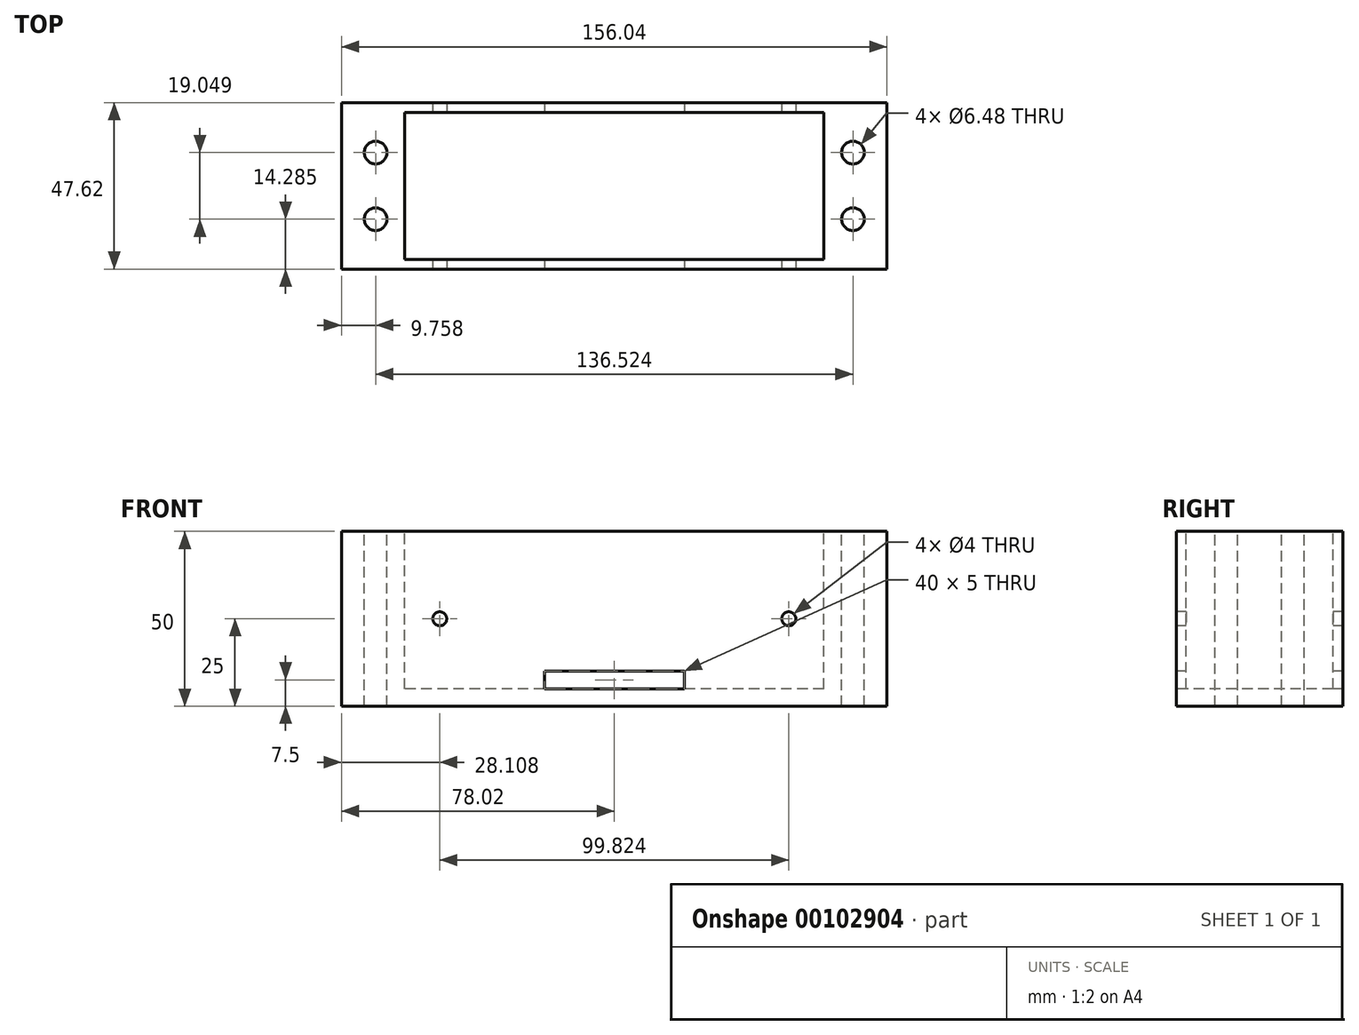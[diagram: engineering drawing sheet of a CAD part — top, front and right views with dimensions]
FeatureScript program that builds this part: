
annotation { "Feature Type Name" : "Feature", "Feature Type Description" : "" }
export const myFeature = defineFeature(function(context is Context, id is Id, definition is map)
    precondition{}
    {
        {
            var Q0;
            Q0=qCreatedBy(makeId("Top.planeOp"),FACE);
            var sketch = newSketch(context, id + "F0", { "sketchPlane" : qUnion([Q0])});
            skLineSegment(sketch, "E0", {"start": v(72.22, -23.01) * mm, "end": v(72.22, -15.86) * mm});
            skLineSegment(sketch, "E1", {"start": v(72.22, -3.19) * mm, "end": v(72.22, 3.17) * mm});
            skLineSegment(sketch, "E2", {"start": v(-68.2, -15.87) * mm, "end": v(-72.23, -15.87) * mm});
            skLineSegment(sketch, "E3", {"start": v(-68.26, 15.87) * mm, "end": v(-72.23, 15.87) * mm});
            skLineSegment(sketch, "E4", {"start": v(68.26, 15.87) * mm, "end": v(72.22, 15.87) * mm});
            skLineSegment(sketch, "E5", {"start": v(-68.26, 3.17) * mm, "end": v(-72.23, 3.17) * mm});
            skLineSegment(sketch, "E6", {"start": v(68.26, 3.17) * mm, "end": v(72.22, 3.17) * mm});
            skLineSegment(sketch, "E7", {"start": v(67.83, -3.19) * mm, "end": v(72.22, -3.19) * mm});
            skArc(sketch, "E8", {"start": v(67.83, -3.19) * mm, "mid": v(61.93, -9.96) * mm, "end": v(68.7, -15.86) * mm});
            skLineSegment(sketch, "E9", {"start": v(68.7, -15.86) * mm, "end": v(72.22, -15.86) * mm});
            skLineSegment(sketch, "E10", {"start": v(-68.33, -3.17) * mm, "end": v(-72.23, -3.17) * mm});
            skArc(sketch, "E11", {"start": v(68.26, 15.87) * mm, "mid": v(61.91, 9.52) * mm, "end": v(68.26, 3.17) * mm});
            skLineSegment(sketch, "E12", {"start": v(72.22, 15.87) * mm, "end": v(72.22, 23.01) * mm});
            skLineSegment(sketch, "E13", {"start": v(-72.23, -3.17) * mm, "end": v(-72.23, 3.17) * mm});
            skLineSegment(sketch, "E14", {"start": v(-72.23, 15.87) * mm, "end": v(-72.23, 23.01) * mm});
            skLineSegment(sketch, "E15", {"start": v(72.22, -23.01) * mm, "end": v(-72.22, -23.01) * mm});
            skArc(sketch, "E16", {"start": v(-68.26, 3.17) * mm, "mid": v(-61.91, 9.52) * mm, "end": v(-68.26, 15.87) * mm});
            skLineSegment(sketch, "E17", {"start": v(-72.23, 23.01) * mm, "end": v(72.22, 23.01) * mm});
            skArc(sketch, "E18", {"start": v(-68.2, -15.87) * mm, "mid": v(-61.91, -9.46) * mm, "end": v(-68.33, -3.17) * mm});
            skLineSegment(sketch, "E19", {"start": v(-72.23, -23.01) * mm, "end": v(-72.23, -15.87) * mm});
            skCircle(sketch, "E20", {"center": v(68.26, -9.52) * mm, "radius": 3.24 * mm});
            skCircle(sketch, "E21", {"center": v(-68.26, 9.52) * mm, "radius": 3.24 * mm});
            skLineSegment(sketch, "E22", {"start": v(-73.03, -23.81) * mm, "end": v(-73.03, 23.81) * mm});
            skCircle(sketch, "E23", {"center": v(-68.26, -9.52) * mm, "radius": 3.24 * mm});
            skLineSegment(sketch, "E24", {"start": v(73.03, -23.81) * mm, "end": v(73.03, 23.81) * mm});
            skLineSegment(sketch, "E25", {"start": v(-73.03, 23.81) * mm, "end": v(73.02, 23.81) * mm});
            skLineSegment(sketch, "E26", {"start": v(73.03, -23.81) * mm, "end": v(-73.02, -23.81) * mm});
            skCircle(sketch, "E27", {"center": v(68.26, 9.52) * mm, "radius": 3.24 * mm});
            skLineSegment(sketch, "E28.bottom", {"start": v(73.03, 23.81) * mm, "end": v(78.03, 23.81) * mm});
            skLineSegment(sketch, "E28.top", {"start": v(73.03, -23.81) * mm, "end": v(78.03, -23.81) * mm});
            skLineSegment(sketch, "E28.left", {"start": v(73.03, 23.81) * mm, "end": v(73.03, -23.81) * mm});
            skLineSegment(sketch, "E28.right", {"start": v(78.03, 23.81) * mm, "end": v(78.03, -23.81) * mm});
            skLineSegment(sketch, "E29.MirrorCS", {"start": v(-73.03, 23.81) * mm, "end": v(-78.03, 23.81) * mm});
            skLineSegment(sketch, "E30.MirrorCS", {"start": v(-78.03, 23.81) * mm, "end": v(-78.03, -23.81) * mm});
            skLineSegment(sketch, "E31.MirrorCS", {"start": v(-73.03, -23.81) * mm, "end": v(-78.03, -23.81) * mm});
            skSolve(sketch);
        }
        {
            var Q0;
            Q0 = qSketchRegion(id + "F0", true);
            var Q1;
            Q1=makeQuery(id+"F0.imprint","IMPRINT",FACE,{"disambiguationData":[TD([[makeQuery(id+"F0.imprint","IMPRINT",EDGE,{"derivedFrom":sQuery(id+"F0.wireOp",EDGE,"E21")}),-1.0]])]});
            var Q2;
            Q2=makeQuery(id+"F0.imprint","IMPRINT",FACE,{"disambiguationData":[TD([[makeQuery(id+"F0.imprint","IMPRINT",EDGE,{"derivedFrom":sQuery(id+"F0.wireOp",EDGE,"E23")}),-1.0]])]});
            var Q3;
            Q3=makeQuery(id+"F0.imprint","IMPRINT",FACE,{"disambiguationData":[TD([[makeQuery(id+"F0.imprint","IMPRINT",EDGE,{"derivedFrom":sQuery(id+"F0.wireOp",EDGE,"E0")}),1.0]])]});
            var Q4;
            Q4=makeQuery(id+"F0.imprint","IMPRINT",FACE,{"disambiguationData":[TD([[makeQuery(id+"F0.imprint","IMPRINT",EDGE,{"derivedFrom":sQuery(id+"F0.wireOp",EDGE,"E27")}),-1.0]])]});
            var Q5;
            Q5=makeQuery(id+"F0.imprint","IMPRINT",FACE,{"disambiguationData":[TD([[makeQuery(id+"F0.imprint","IMPRINT",EDGE,{"derivedFrom":sQuery(id+"F0.wireOp",EDGE,"E20")}),-1.0]])]});
            extrude(context, id + "F1", {"entities" : qUnion([Q0, Q1, Q2, Q3, Q4, Q5]), "oppositeDirection" : true, "depth" : 50 * mm});
        }
        {
            var Q0;
            Q0=makeQuery(id+"F0.imprint","IMPRINT",FACE,{"disambiguationData":[TD([[makeQuery(id+"F0.imprint","IMPRINT",EDGE,{"derivedFrom":sQuery(id+"F0.wireOp",EDGE,"E0")}),1.0]])]});
            var sketch = newSketch(context, id + "F2", { "sketchPlane" : qUnion([Q0])});
            skLineSegment(sketch, "E32.bottom", {"start": v(59.91, 21.01) * mm, "end": v(-59.91, 21.01) * mm});
            skLineSegment(sketch, "E32.top", {"start": v(59.91, -21.01) * mm, "end": v(-59.91, -21.01) * mm});
            skLineSegment(sketch, "E32.left", {"start": v(59.91, 21.01) * mm, "end": v(59.91, -21.01) * mm});
            skLineSegment(sketch, "E32.right", {"start": v(-59.91, 21.01) * mm, "end": v(-59.91, -21.01) * mm});
            skPoint(sketch, "E32.middle", {"position": v(0, 0) * mm});
            skSolve(sketch);
        }
        {
            var Q0;
            Q0 = qSketchRegion(id + "F2", true);
            extrude(context, id + "F3", {"entities" : qUnion([Q0]), "operationType" : NewBodyOperationType.REMOVE, "oppositeDirection" : true, "depth" : 45 * mm});
        }
        {
            var Q0;
            Q0=sQuery(id+"F0.wireOp",VERTEX,"E16.center");
            var Q1;
            Q1=sQuery(id+"F0.wireOp",VERTEX,"E18.center");
            var Q2;
            Q2=sQuery(id+"F0.wireOp",VERTEX,"E11.center");
            var Q3;
            Q3=sQuery(id+"F0.wireOp",VERTEX,"E8.center");
            var Q4;
            Q4=makeQuery(id+"F1.opExtrude","SWEPT_BODY",BODY,{"disambiguationData":[OSD([sQuery(id+"F0.wireOp",EDGE,"E25"),sQuery(id+"F0.wireOp",EDGE,"E26"),sQuery(id+"F0.wireOp",EDGE,"E28.bottom"),sQuery(id+"F0.wireOp",EDGE,"E28.top"),sQuery(id+"F0.wireOp",EDGE,"E28.right"),sQuery(id+"F0.wireOp",EDGE,"E29.MirrorCS"),sQuery(id+"F0.wireOp",EDGE,"E30.MirrorCS"),sQuery(id+"F0.wireOp",EDGE,"E31.MirrorCS")])]});
            hole(context, id + "F4", {"style" : HoleStyle.SIMPLE, "endStyle" : HoleEndStyle.BLIND, "holeDiameter" : 5.6 * mm, "holeDepth" : 20 * mm, "locations" : qUnion([Q0, Q1, Q2, Q3]), "scope" : qUnion([Q4])});
        }
        {
            var Q0;
            Q0=makeQuery(id+"F1.opExtrude","SWEPT_FACE",FACE,{"disambiguationData":[OSD([sQuery(id+"F0.wireOp",EDGE,"E26"),sQuery(id+"F0.wireOp",EDGE,"E28.top"),sQuery(id+"F0.wireOp",EDGE,"E31.MirrorCS")])]});
            var sketch = newSketch(context, id + "F5", { "sketchPlane" : qUnion([Q0])});
            skLineSegment(sketch, "E33.bottom", {"start": v(20, -40) * mm, "end": v(-20, -40) * mm});
            skLineSegment(sketch, "E33.top", {"start": v(20, -45) * mm, "end": v(-20, -45) * mm});
            skLineSegment(sketch, "E33.left", {"start": v(20, -40) * mm, "end": v(20, -45) * mm});
            skLineSegment(sketch, "E33.right", {"start": v(-20, -40) * mm, "end": v(-20, -45) * mm});
            skPoint(sketch, "E33.middle", {"position": v(0, -42.5) * mm});
            skPoint(sketch, "E33.middle.positionSnap0", {"position": v(0, -50) * mm});
            skPoint(sketch, "E33.centerSnap0", {"position": v(0, -50) * mm});
            skPoint(sketch, "E34", {"position": v(-49.91, -25) * mm});
            skPoint(sketch, "E35.MirrorP", {"position": v(49.91, -25) * mm});
            skSolve(sketch);
        }
        {
            var Q0;
            Q0 = qSketchRegion(id + "F5", true);
            extrude(context, id + "F6", {"entities" : qUnion([Q0]), "operationType" : NewBodyOperationType.REMOVE, "endBound" : BoundingType.THROUGH_ALL, "oppositeDirection" : true, "depth" : 25 * mm});
        }
        {
            var Q0;
            Q0=sQuery(id+"F5.wireOp",VERTEX,"E34");
            var Q1;
            Q1=sQuery(id+"F5.wireOp",VERTEX,"E35.MirrorP");
            var Q2;
            Q2=makeQuery(id+"F1.opExtrude","SWEPT_BODY",BODY,{"disambiguationData":[OSD([sQuery(id+"F0.wireOp",EDGE,"E25"),sQuery(id+"F0.wireOp",EDGE,"E26"),sQuery(id+"F0.wireOp",EDGE,"E28.bottom"),sQuery(id+"F0.wireOp",EDGE,"E28.top"),sQuery(id+"F0.wireOp",EDGE,"E28.right"),sQuery(id+"F0.wireOp",EDGE,"E29.MirrorCS"),sQuery(id+"F0.wireOp",EDGE,"E30.MirrorCS"),sQuery(id+"F0.wireOp",EDGE,"E31.MirrorCS")])]});
            hole(context, id + "F7", {"style" : HoleStyle.SIMPLE, "endStyle" : HoleEndStyle.THROUGH, "holeDiameter" : 4 * mm, "locations" : qUnion([Q0, Q1]), "scope" : qUnion([Q2]), "isTappedThrough" : true});
        }
    });
